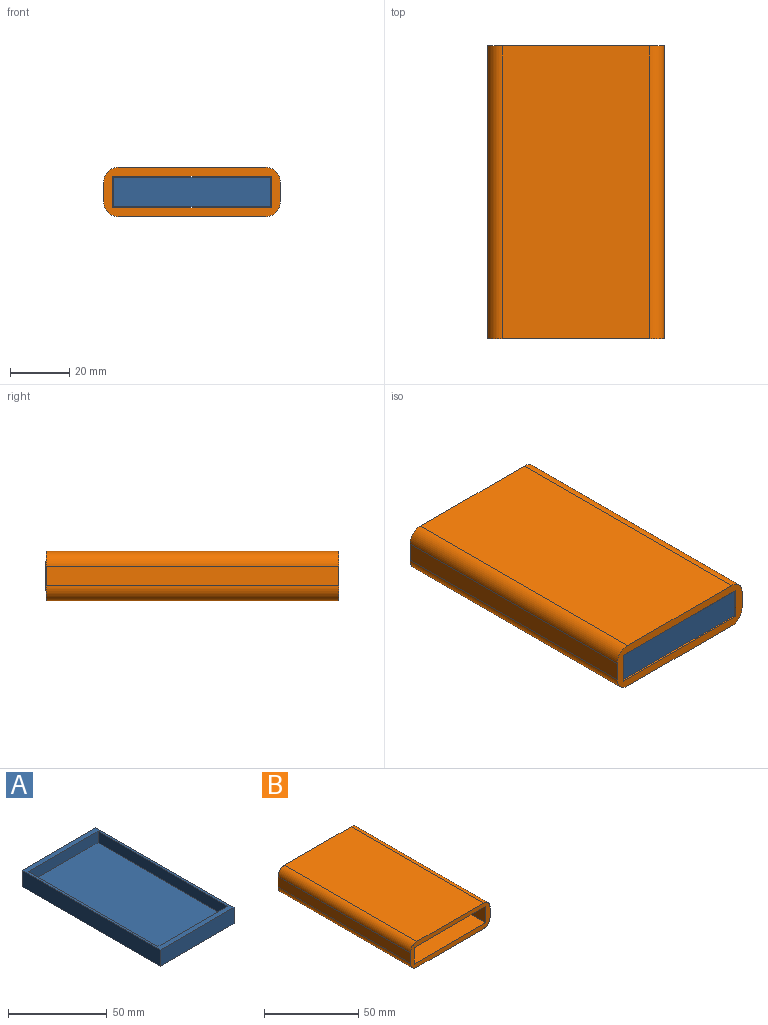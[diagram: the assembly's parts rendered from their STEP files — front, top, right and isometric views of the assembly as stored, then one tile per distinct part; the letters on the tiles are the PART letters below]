
ASSEMBLY  parts=2 mates=1
PART A: 11 faces, bbox 53x99x10 mm
  f0: plane 53x10mm, normal (0,1,0), area 530mm2, adj f1,f3,f4,f9
  f1: plane 99x10mm, normal (-1,0,0), area 990mm2, adj f0,f2,f4,f9
  f2: plane 53x10mm, normal (0,-1,0), area 530mm2, adj f1,f3,f4,f9
  f3: plane 99x10mm, normal (1,0,0), area 990mm2, adj f0,f2,f4,f9
  f4: plane 99x53mm, normal (0,0,-1), area 5247mm2, adj f0,f1,f2,f3
  f5: plane 93x7mm, normal (-1,0,0), area 651mm2, adj f6,f8,f9,f10
  f6: plane 50x7mm, normal (0,1,0), area 350mm2, adj f5,f7,f9,f10
  f7: plane 93x7mm, normal (1,0,0), area 651mm2, adj f6,f8,f9,f10
  f8: plane 50x7mm, normal (0,-1,0), area 350mm2, adj f5,f7,f9,f10
  f9: plane 99x53mm, normal (0,0,1), area 597mm2, adj f0,f1,f2,f3,f5,f6,f7,f8
  f10: plane 93x50mm, normal (0,0,1), area 4650mm2, adj f5,f6,f7,f8
PART B: 14 faces, bbox 59.7x99x16.7 mm
  f0: plane 59.7x16.7mm, normal (0,-1,0), area 400.9mm2, adj f1,f2,f3,f5,f6,f7,f8,f9
  f1: plane 99x49.7mm, normal (0,0,-1), area 4920.3mm2, adj f0,f4,f10,f11
  f2: plane 99x10.7mm, normal (1,0,0), area 1059.3mm2, adj f0,f3,f4,f8
  f3: plane 99x53.7mm, normal (0,0,1), area 5316.3mm2, adj f0,f2,f4,f9
  f4: plane 59.7x16.7mm, normal (0,1,0), area 400.9mm2, adj f1,f2,f3,f5,f6,f7,f8,f9
  f5: plane 99x6.7mm, normal (1,0,0), area 663.3mm2, adj f0,f4,f10,f12
  f6: plane 99x6.7mm, normal (-1,0,0), area 663.3mm2, adj f0,f4,f11,f13
  f7: plane 99x49.7mm, normal (0,0,1), area 4920.3mm2, adj f0,f4,f12,f13
  f8: plane 99x53.7mm, normal (0,0,-1), area 5316.3mm2, adj f0,f2,f4,f9
  f9: plane 99x10.7mm, normal (-1,0,0), area 1059.3mm2, adj f0,f3,f4,f8
  f10: cylinder r=5mm len=99mm, axis (0,1,0), area 777.5mm2, adj f0,f1,f4,f5
  f11: cylinder r=5mm len=99mm, axis (0,1,0), area 777.5mm2, adj f0,f1,f4,f6
  f12: cylinder r=5mm len=99mm, axis (0,1,0), area 777.5mm2, adj f0,f4,f5,f7
  f13: cylinder r=5mm len=99mm, axis (0,1,0), area 777.5mm2, adj f0,f4,f6,f7
PLACE A t=(-0.36,0.23,-1.82)mm
PLACE B t=(-0.36,-0.09,-1.82)mm fixed
MATE slider A.f2 <-> B.f0  axis (0,-1,0) through (-0.36,-49.27,0.18)mm
